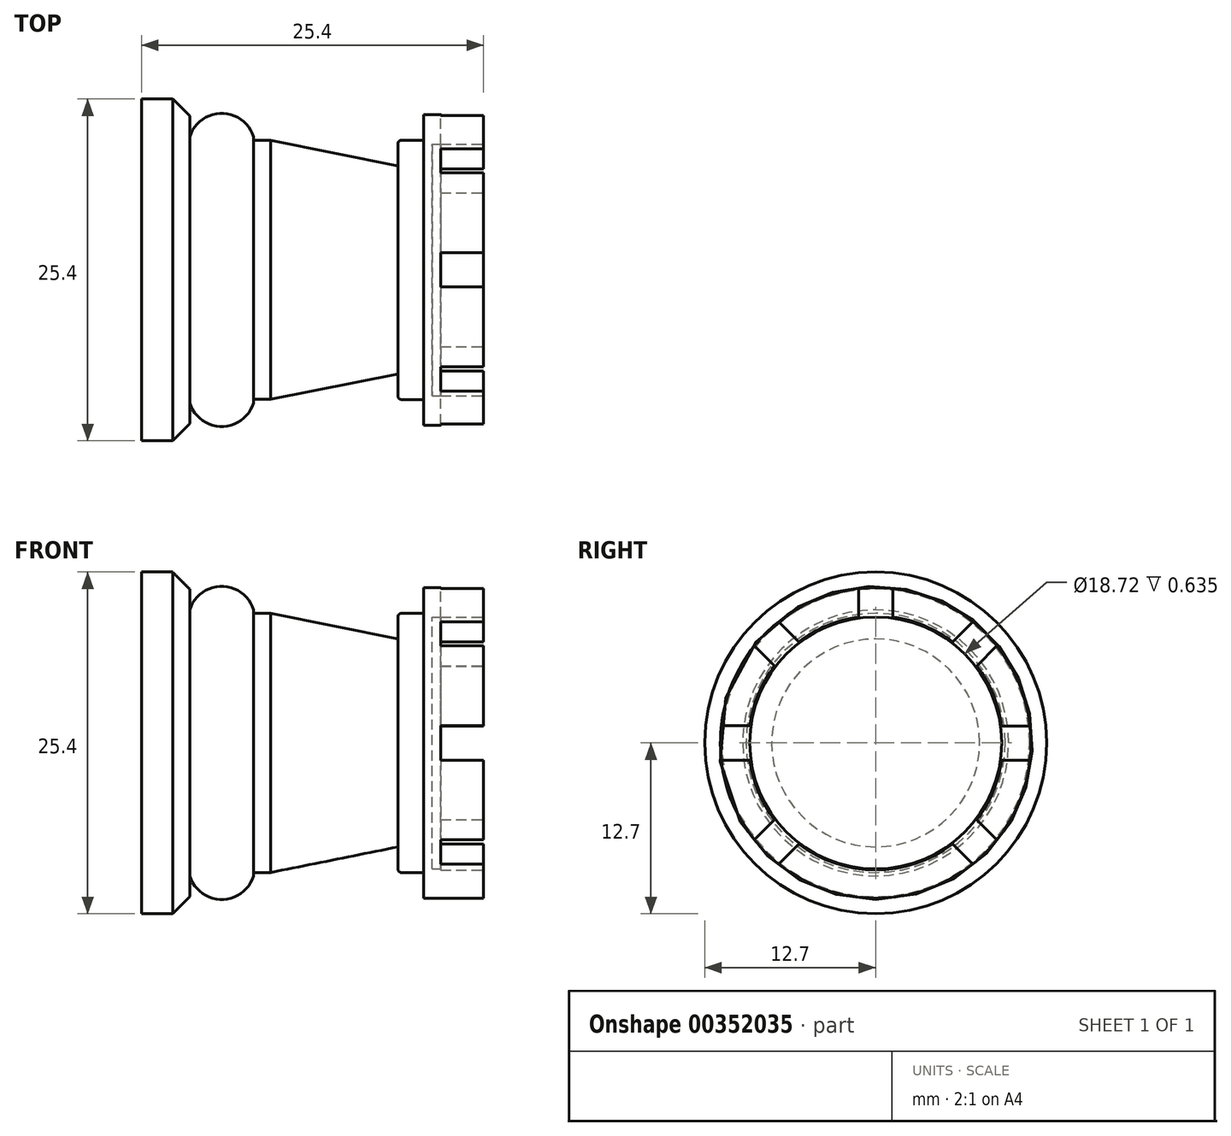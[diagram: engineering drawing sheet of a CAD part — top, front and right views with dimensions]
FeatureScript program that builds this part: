
annotation { "Feature Type Name" : "Feature", "Feature Type Description" : "" }
export const myFeature = defineFeature(function(context is Context, id is Id, definition is map)
    precondition{}
    {
        {
            var Q0;
            Q0=qCreatedBy(makeId("Front.planeOp"),FACE);
            var sketch = newSketch(context, id + "F0", { "sketchPlane" : qUnion([Q0])});
            skLineSegment(sketch, "E0", {"start": v(0, 0) * mm, "end": v(-25.4, 0) * mm});
            skLineSegment(sketch, "E1", {"start": v(-25.4, 0) * mm, "end": v(-25.4, 12.7) * mm});
            skLineSegment(sketch, "E2", {"start": v(-25.4, 12.7) * mm, "end": v(-21.83, 12.7) * mm});
            skLineSegment(sketch, "E3", {"start": v(-21.83, 12.7) * mm, "end": v(-21.83, 9.88) * mm});
            skArc(sketch, "E4", {"start": v(-17.07, 9.88) * mm, "mid": v(-19.45, 11.63) * mm, "end": v(-21.83, 9.88) * mm});
            skLineSegment(sketch, "E5", {"start": v(-15.8, 9.63) * mm, "end": v(-6.35, 7.73) * mm});
            skLineSegment(sketch, "E6", {"start": v(-6.35, 7.73) * mm, "end": v(-6.35, 9.63) * mm});
            skLineSegment(sketch, "E7", {"start": v(-6.35, 9.63) * mm, "end": v(-4.45, 9.63) * mm});
            skLineSegment(sketch, "E8", {"start": v(-4.45, 9.63) * mm, "end": v(-4.45, 11.54) * mm});
            skLineSegment(sketch, "E9", {"start": v(-4.45, 11.54) * mm, "end": v(0, 11.54) * mm});
            skLineSegment(sketch, "E10", {"start": v(0, 11.54) * mm, "end": v(0, 0) * mm});
            skLineSegment(sketch, "E11", {"start": v(-17.07, 9.88) * mm, "end": v(-17.07, 0) * mm});
            skLineSegment(sketch, "E12", {"start": v(-15.8, 0) * mm, "end": v(-15.8, 9.63) * mm});
            skLineSegment(sketch, "E13", {"start": v(-15.8, 9.63) * mm, "end": v(-17.07, 9.63) * mm});
            skSolve(sketch);
        }
        {
            var Q0;
            Q0=makeQuery(id+"F0.imprint","IMPRINT",FACE,{"disambiguationData":[TD([[makeQuery(id+"F0.imprint","IMPRINT",EDGE,{"derivedFrom":sQuery(id+"F0.wireOp",EDGE,"E5")}),-1.0]])]});
            var Q1;
            {var subQ3=sQuery(id+"F0.wireOp",EDGE,"E12");Q1=makeQuery(id+"F0.imprint","IMPRINT",FACE,{"disambiguationData":[TD([[makeQuery(id+"F0.imprint","IMPRINT",EDGE,{"derivedFrom":subQ3}),1.0]])]});}
            var Q2;
            {var subQ0=sQuery(id+"F0.wireOp",EDGE,"E1");Q2=makeQuery(id+"F0.imprint","IMPRINT",FACE,{"disambiguationData":[TD([[makeQuery(id+"F0.imprint","IMPRINT",EDGE,{"derivedFrom":subQ0}),-1.0]])]});}
            var Q3;
            Q3=sQuery(id+"F0.wireOp",EDGE,"E0");
            revolve(context, id + "F1", {"entities" : qUnion([Q0, Q1, Q2]), "axis" : qUnion([Q3]), "revolveType" : RevolveType.FULL});
        }
        {
            var Q0;
            Q0=makeQuery(id+"F1.opRevolve","SWEPT_FACE",FACE,{"disambiguationData":[OSD([sQuery(id+"F0.wireOp",EDGE,"E10")])]});
            var sketch = newSketch(context, id + "F2", { "sketchPlane" : qUnion([Q0])});
            skCircle(sketch, "E14", {"center": v(0, 0) * mm, "radius": 9.44 * mm});
            skPoint(sketch, "E15.start.orphan", {"position": v(-1.27, -9.35) * mm});
            skPoint(sketch, "E16.end.orphan", {"position": v(-1.27, 11.46) * mm});
            skLineSegment(sketch, "E17", {"start": v(-1.27, -9.35) * mm, "end": v(-1.27, -11.46) * mm});
            skLineSegment(sketch, "E18", {"start": v(-1.27, -11.46) * mm, "end": v(-1.27, -9.35) * mm});
            skLineSegment(sketch, "E19", {"start": v(-11.46, -1.27) * mm, "end": v(-9.35, -1.27) * mm});
            skLineSegment(sketch, "E20.MirrorCS", {"start": v(1.25, -11.51) * mm, "end": v(1.26, -9.35) * mm});
            skLineSegment(sketch, "E21.MirrorCS", {"start": v(-11.48, 1.28) * mm, "end": v(-9.35, 1.27) * mm});
            skLineSegment(sketch, "E22.trimOffspring", {"start": v(9.35, -1.27) * mm, "end": v(11.46, -1.27) * mm});
            skPoint(sketch, "E23.orphan", {"position": v(0, 11.54) * mm});
            skLineSegment(sketch, "E24.trimOffspring", {"start": v(-1.26, 9.35) * mm, "end": v(-1.27, 11.46) * mm});
            skLineSegment(sketch, "E25.trimOffspring", {"start": v(1.27, 9.35) * mm, "end": v(1.28, 11.58) * mm});
            skLineSegment(sketch, "E26.trimOffspring", {"start": v(9.35, 1.26) * mm, "end": v(11.57, 1.25) * mm});
            skLineSegment(sketch, "E27", {"start": v(7.51, 5.71) * mm, "end": v(9, 7.2) * mm});
            skLineSegment(sketch, "E28.MirrorCS", {"start": v(5.71, 7.51) * mm, "end": v(7.26, 9.06) * mm});
            skLineSegment(sketch, "E29", {"start": v(-5.72, -7.5) * mm, "end": v(-7.2, -9) * mm});
            skLineSegment(sketch, "E30.MirrorCS", {"start": v(-7.51, -5.71) * mm, "end": v(-9, -7.2) * mm});
            skLineSegment(sketch, "E31", {"start": v(-5.71, 7.51) * mm, "end": v(-7.2, 9) * mm});
            skLineSegment(sketch, "E32.MirrorCS", {"start": v(-7.51, 5.71) * mm, "end": v(-9, 7.2) * mm});
            skLineSegment(sketch, "E33", {"start": v(7.2, -9) * mm, "end": v(5.71, -7.51) * mm});
            skLineSegment(sketch, "E34.MirrorCS", {"start": v(9, -7.2) * mm, "end": v(7.51, -5.71) * mm});
            skSolve(sketch);
        }
        {
            var Q0;
            Q0=makeQuery(id+"F1.opRevolve","SWEPT_EDGE",EDGE,{"disambiguationData":[OSD([sQuery(id+"F0.wireOp",EDGE,"E2"),sQuery(id+"F0.wireOp",EDGE,"E3")])]});
            chamfer(context, id + "F3", {"entities" : qUnion([Q0]), "width" : 1.27 * mm, "tangentPropagation" : true});
        }
        {
            var Q0;
            Q0=makeQuery(id+"F1.opRevolve","SWEPT_EDGE",EDGE,{"disambiguationData":[OSD([sQuery(id+"F0.wireOp",EDGE,"E6"),sQuery(id+"F0.wireOp",EDGE,"E7")])]});
            fillet(context, id + "F4", {"entities" : qUnion([Q0]), "radius" : 0.25 * mm, "tangentPropagation" : true, "allowEdgeOverflow" : false});
        }
        {
            var Q0;
            {var subQ0=sQuery(id+"F2.wireOp",EDGE,"E31");Q0=makeQuery(id+"F2.imprint","IMPRINT",FACE,{"disambiguationData":[TD([[makeQuery(id+"F2.imprint","IMPRINT",EDGE,{"derivedFrom":subQ0}),1.0]])]});}
            var Q1;
            {var subQ0=sQuery(id+"F2.wireOp",EDGE,"E24.trimOffspring");Q1=makeQuery(id+"F2.imprint","IMPRINT",FACE,{"disambiguationData":[TD([[makeQuery(id+"F2.imprint","IMPRINT",EDGE,{"derivedFrom":subQ0}),-1.0]])]});}
            var Q2;
            {var subQ0=sQuery(id+"F2.wireOp",EDGE,"E27");Q2=makeQuery(id+"F2.imprint","IMPRINT",FACE,{"disambiguationData":[TD([[makeQuery(id+"F2.imprint","IMPRINT",EDGE,{"derivedFrom":subQ0}),1.0]])]});}
            var Q3;
            {var subQ0=sQuery(id+"F2.wireOp",EDGE,"E22.trimOffspring");Q3=makeQuery(id+"F2.imprint","IMPRINT",FACE,{"disambiguationData":[TD([[makeQuery(id+"F2.imprint","IMPRINT",EDGE,{"derivedFrom":subQ0}),1.0]])]});}
            var Q4;
            {var subQ0=sQuery(id+"F2.wireOp",EDGE,"E33");Q4=makeQuery(id+"F2.imprint","IMPRINT",FACE,{"disambiguationData":[TD([[makeQuery(id+"F2.imprint","IMPRINT",EDGE,{"derivedFrom":subQ0}),-1.0]])]});}
            var Q5;
            {var subQ0=sQuery(id+"F2.wireOp",EDGE,"E18");Q5=makeQuery(id+"F2.imprint","IMPRINT",FACE,{"disambiguationData":[TD([[makeQuery(id+"F2.imprint","IMPRINT",EDGE,{"derivedFrom":subQ0}),-1.0]])]});}
            var Q6;
            {var subQ0=sQuery(id+"F2.wireOp",EDGE,"E29");Q6=makeQuery(id+"F2.imprint","IMPRINT",FACE,{"disambiguationData":[TD([[makeQuery(id+"F2.imprint","IMPRINT",EDGE,{"derivedFrom":subQ0}),-1.0]])]});}
            var Q7;
            {var subQ0=sQuery(id+"F2.wireOp",EDGE,"E19");Q7=makeQuery(id+"F2.imprint","IMPRINT",FACE,{"disambiguationData":[TD([[makeQuery(id+"F2.imprint","IMPRINT",EDGE,{"derivedFrom":subQ0}),1.0]])]});}
            var Q8;
            {var subQ0=sQuery(id+"F2.wireOp",EDGE,"E14");var subQ8=makeQuery(id+"F2.imprint","INTERSECT",VERTEX,{"derivedFrom":[subQ0,sQuery(id+"F2.wireOp",EDGE,"E26.trimOffspring")]});Q8=makeQuery(id+"F2.imprint","IMPRINT",FACE,{"disambiguationData":[TD([[makeQuery(id+"F2.imprint","IMPRINT",EDGE,{"disambiguationData":[TD([[subQ8,-1.0]])],"derivedFrom":subQ0}),1.0]])]});}
            extrude(context, id + "F5", {"entities" : qUnion([Q0, Q1, Q2, Q3, Q4, Q5, Q6, Q7, Q8]), "operationType" : NewBodyOperationType.REMOVE, "oppositeDirection" : true, "depth" : 3.17 * mm});
        }
        {
            var Q0;
            Q0=makeQuery(id+"F5.boolean.opBoolean","COPY",FACE,{"derivedFrom":makeQuery(id+"F5.opExtrude","CAP_FACE",FACE,{"disambiguationData":[OSD([sQuery(id+"F0.wireOp",EDGE,"E9"),sQuery(id+"F0.wireOp",EDGE,"E10"),sQuery(id+"F2.wireOp",EDGE,"E14"),sQuery(id+"F2.wireOp",EDGE,"E18"),sQuery(id+"F2.wireOp",EDGE,"E19"),sQuery(id+"F2.wireOp",EDGE,"E20.MirrorCS"),sQuery(id+"F2.wireOp",EDGE,"E21.MirrorCS"),sQuery(id+"F2.wireOp",EDGE,"E22.trimOffspring"),sQuery(id+"F2.wireOp",EDGE,"E24.trimOffspring"),sQuery(id+"F2.wireOp",EDGE,"E25.trimOffspring"),sQuery(id+"F2.wireOp",EDGE,"E26.trimOffspring"),sQuery(id+"F2.wireOp",EDGE,"E27"),sQuery(id+"F2.wireOp",EDGE,"E28.MirrorCS"),sQuery(id+"F2.wireOp",EDGE,"E29"),sQuery(id+"F2.wireOp",EDGE,"E30.MirrorCS"),sQuery(id+"F2.wireOp",EDGE,"E31"),sQuery(id+"F2.wireOp",EDGE,"E32.MirrorCS"),sQuery(id+"F2.wireOp",EDGE,"E33"),sQuery(id+"F2.wireOp",EDGE,"E34.MirrorCS")])],"isStart":false})});
            var sketch = newSketch(context, id + "F6", { "sketchPlane" : qUnion([Q0])});
            skCircle(sketch, "E35", {"center": v(0, 0) * mm, "radius": 9.36 * mm});
            skSolve(sketch);
        }
        {
            var Q0;
            Q0=makeQuery(id+"F6.imprint","IMPRINT",FACE,{"disambiguationData":[TD([[makeQuery(id+"F6.imprint","IMPRINT",EDGE,{"derivedFrom":sQuery(id+"F6.wireOp",EDGE,"E35")}),1.0]])]});
            extrude(context, id + "F7", {"entities" : qUnion([Q0]), "operationType" : NewBodyOperationType.REMOVE, "oppositeDirection" : true, "depth" : 0.64 * mm});
        }
    });
